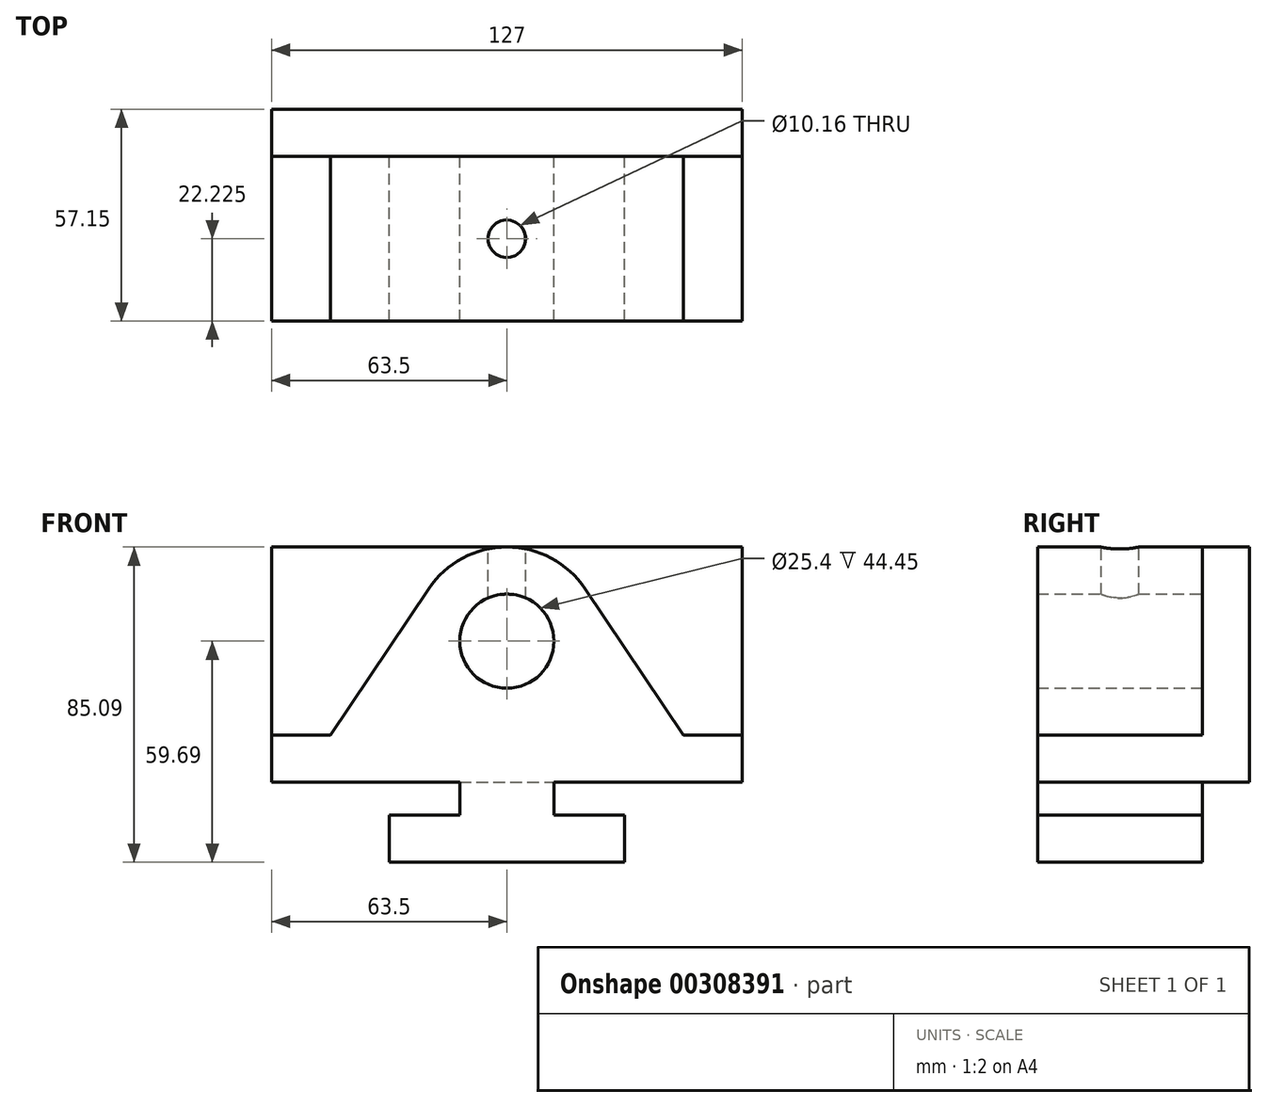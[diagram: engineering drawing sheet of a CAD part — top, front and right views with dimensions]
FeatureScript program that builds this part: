
annotation { "Feature Type Name" : "Feature", "Feature Type Description" : "" }
export const myFeature = defineFeature(function(context is Context, id is Id, definition is map)
    precondition{}
    {
        {
            var Q0;
            Q0=qCreatedBy(makeId("Front.planeOp"),FACE);
            var sketch = newSketch(context, id + "F0", { "sketchPlane" : qUnion([Q0])});
            skLineSegment(sketch, "E0", {"start": v(0, -21.59) * mm, "end": v(-31.75, -21.59) * mm});
            skLineSegment(sketch, "E1", {"start": v(-31.75, -21.59) * mm, "end": v(-31.75, -8.89) * mm});
            skLineSegment(sketch, "E2", {"start": v(-31.75, -8.89) * mm, "end": v(-12.7, -8.89) * mm});
            skLineSegment(sketch, "E3", {"start": v(-12.7, -8.89) * mm, "end": v(-12.7, 0) * mm});
            skLineSegment(sketch, "E4", {"start": v(-12.7, 0) * mm, "end": v(-63.5, 0) * mm});
            skLineSegment(sketch, "E5", {"start": v(-63.5, 0) * mm, "end": v(-63.5, 12.7) * mm});
            skLineSegment(sketch, "E6", {"start": v(-63.5, 12.7) * mm, "end": v(-47.63, 12.7) * mm});
            skLineSegment(sketch, "E7", {"start": v(-47.63, 12.7) * mm, "end": v(-21.1, 52.25) * mm});
            skLineSegment(sketch, "E8", {"start": v(21.1, 52.25) * mm, "end": v(47.62, 12.7) * mm});
            skLineSegment(sketch, "E9", {"start": v(47.62, 12.7) * mm, "end": v(63.5, 12.7) * mm});
            skLineSegment(sketch, "E10", {"start": v(63.5, 12.7) * mm, "end": v(63.5, 0) * mm});
            skLineSegment(sketch, "E11", {"start": v(63.5, 0) * mm, "end": v(12.7, 0) * mm});
            skLineSegment(sketch, "E12", {"start": v(12.7, 0) * mm, "end": v(12.7, -8.9) * mm});
            skLineSegment(sketch, "E13", {"start": v(12.7, -8.9) * mm, "end": v(31.75, -8.9) * mm});
            skLineSegment(sketch, "E14", {"start": v(31.75, -8.9) * mm, "end": v(31.75, -21.6) * mm});
            skLineSegment(sketch, "E15", {"start": v(31.75, -21.6) * mm, "end": v(0, -21.59) * mm});
            skArc(sketch, "E16", {"start": v(-21.1, 52.25) * mm, "mid": v(0, 63.5) * mm, "end": v(21.1, 52.25) * mm});
            skCircle(sketch, "E17", {"center": v(0, 38.1) * mm, "radius": 12.7 * mm});
            skSolve(sketch);
        }
        {
            var Q0;
            Q0 = qSketchRegion(id + "F0", true);
            extrude(context, id + "F1", {"entities" : qUnion([Q0]), "depth" : 44.45 * mm});
        }
        {
            var Q0;
            Q0=makeQuery(id+"F1.opExtrude","CAP_FACE",FACE,{"disambiguationData":[OSD([sQuery(id+"F0.wireOp",EDGE,"E0"),sQuery(id+"F0.wireOp",EDGE,"E1"),sQuery(id+"F0.wireOp",EDGE,"E2"),sQuery(id+"F0.wireOp",EDGE,"E3"),sQuery(id+"F0.wireOp",EDGE,"E4"),sQuery(id+"F0.wireOp",EDGE,"E5"),sQuery(id+"F0.wireOp",EDGE,"E6"),sQuery(id+"F0.wireOp",EDGE,"E7"),sQuery(id+"F0.wireOp",EDGE,"E8"),sQuery(id+"F0.wireOp",EDGE,"E9"),sQuery(id+"F0.wireOp",EDGE,"E10"),sQuery(id+"F0.wireOp",EDGE,"E11"),sQuery(id+"F0.wireOp",EDGE,"E12"),sQuery(id+"F0.wireOp",EDGE,"E13"),sQuery(id+"F0.wireOp",EDGE,"E14"),sQuery(id+"F0.wireOp",EDGE,"E15"),sQuery(id+"F0.wireOp",EDGE,"E16"),sQuery(id+"F0.wireOp",EDGE,"E17")])],"isStart":true});
            var sketch = newSketch(context, id + "F2", { "sketchPlane" : qUnion([Q0])});
            skLineSegment(sketch, "E18", {"start": v(-63.5, 0) * mm, "end": v(-63.5, 63.5) * mm});
            skPoint(sketch, "E18.endSnap0", {"position": v(0, 63.5) * mm});
            skLineSegment(sketch, "E19", {"start": v(-63.5, 63.5) * mm, "end": v(0, 63.5) * mm});
            skLineSegment(sketch, "E20", {"start": v(0, 63.5) * mm, "end": v(63.5, 63.5) * mm});
            skLineSegment(sketch, "E21", {"start": v(63.5, 63.5) * mm, "end": v(63.5, 12.7) * mm});
            skLineSegment(sketch, "E22", {"start": v(63.5, 12.7) * mm, "end": v(63.5, 0) * mm});
            skLineSegment(sketch, "E23", {"start": v(63.5, 0) * mm, "end": v(-63.5, 0) * mm});
            skSolve(sketch);
        }
        {
            var Q0;
            Q0 = qSketchRegion(id + "F2", true);
            extrude(context, id + "F3", {"entities" : qUnion([Q0]), "operationType" : NewBodyOperationType.ADD, "depth" : 12.7 * mm});
        }
        {
            var Q0;
            Q0=makeQuery(id+"F3.opExtrude","SWEPT_FACE",FACE,{"disambiguationData":[OSD([sQuery(id+"F2.wireOp",EDGE,"E19")])]});
            var sketch = newSketch(context, id + "F4", { "sketchPlane" : qUnion([Q0])});
            skCircle(sketch, "E24", {"center": v(0, -22.23) * mm, "radius": 5.08 * mm});
            skSolve(sketch);
        }
        {
            var Q0;
            Q0 = qSketchRegion(id + "F4", true);
            var Q1;
            Q1=makeQuery(id+"F1.opExtrude","SWEPT_FACE",FACE,{"disambiguationData":[OSD([sQuery(id+"F0.wireOp",EDGE,"E17")])]});
            extrude(context, id + "F5", {"entities" : qUnion([Q0]), "operationType" : NewBodyOperationType.REMOVE, "endBound" : BoundingType.UP_TO_SURFACE, "oppositeDirection" : true, "endBoundEntityFace" : qUnion([Q1]), "depth" : 25.4 * mm});
        }
    });
